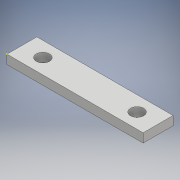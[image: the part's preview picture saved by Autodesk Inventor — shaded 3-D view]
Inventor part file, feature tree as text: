
AUTODESK INVENTOR PART (.ipt)
format: ipt  version: 2017 (Build 210142000, 142)  size: 104,448 bytes
history: native  units: mm
features: sketch x3, extrude x1, hole x1
ambient origin geometry x8: Origin, YZ Plane, XZ Plane, XY Plane, X Axis, Y Axis, Z Axis, Center Point
bodies: Solid1 (feature_tree)
feature tree (5):
  extrude  "Extrusion1"  Depth=10.0mm
  sketch  "Sketch2"  dims[d2=3.0mm d3=0.0mm d4=7.0mm]
  sketch  "Sketch3"  dims[d5=7.0mm d6=5.0mm d7=5.0mm d8=4.4mm d9=6.0mm d10=4.0mm d11=2.0mm d12=90.0deg d13=8.0mm d14=20.594885mm]
  hole  "Hole1"  [1 undecoded]
  sketch  "Sketch1"  dims[d0=45.5mm d1=10.0mm]
note: 1 required parameter value undecoded (feature->parameter linkage not recoverable at this tier; creation-order binding heuristic only, values carry confidence <= 0.55)
